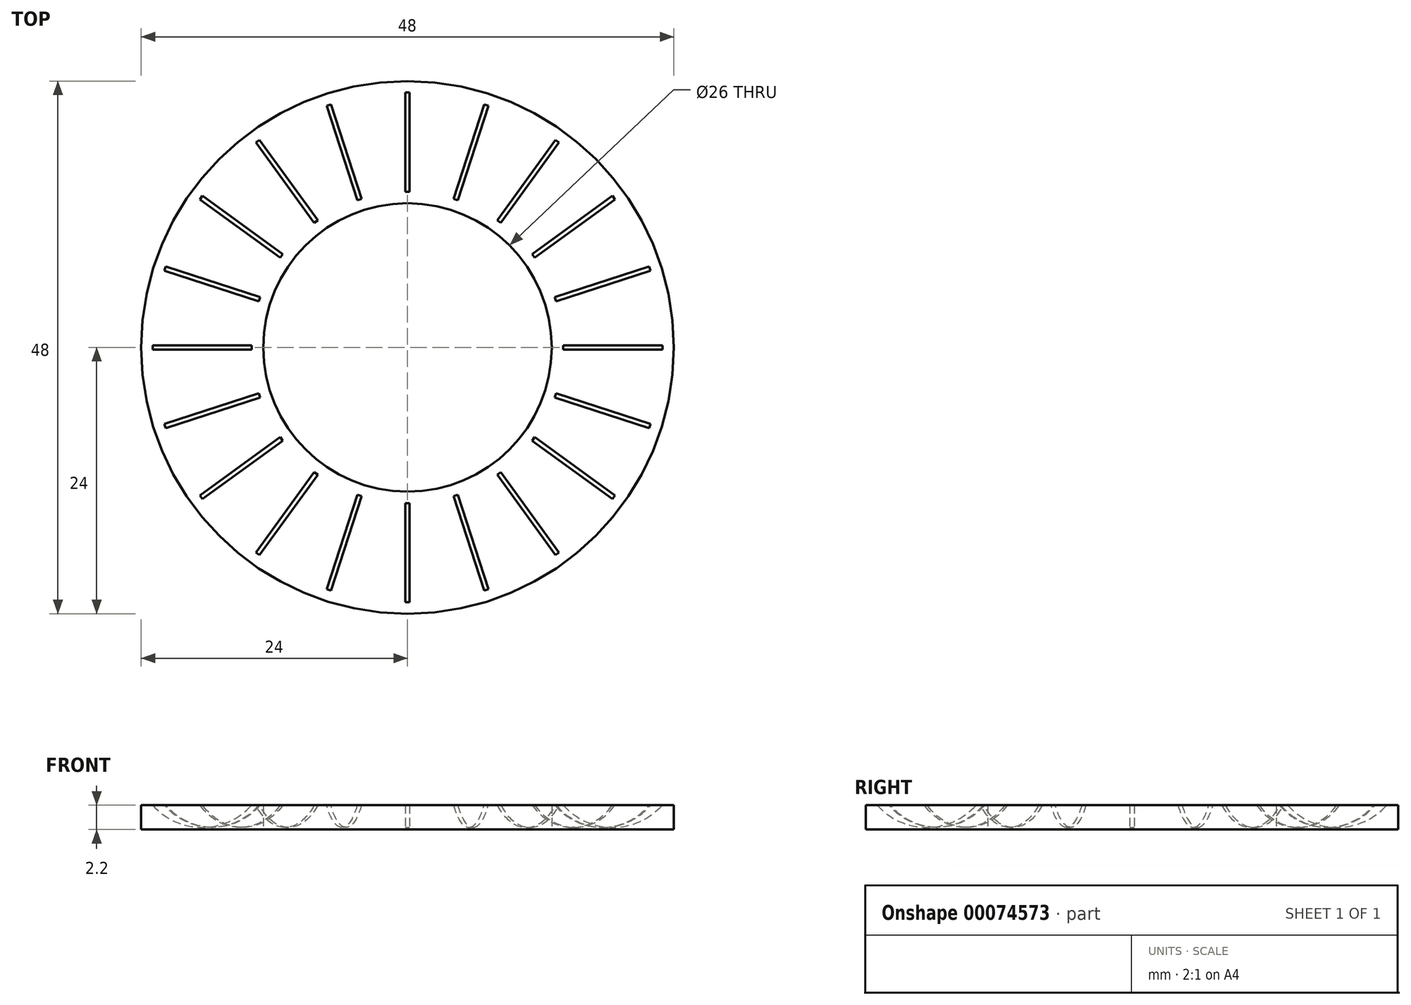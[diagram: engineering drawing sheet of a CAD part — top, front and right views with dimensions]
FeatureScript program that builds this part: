
annotation { "Feature Type Name" : "Feature", "Feature Type Description" : "" }
export const myFeature = defineFeature(function(context is Context, id is Id, definition is map)
    precondition{}
    {
        {
            var Q0;
            Q0=qCreatedBy(makeId("Top.planeOp"),FACE);
            var sketch = newSketch(context, id + "F0", { "sketchPlane" : qUnion([Q0])});
            skCircle(sketch, "E0", {"center": v(0, 0) * mm, "radius": 13 * mm});
            skCircle(sketch, "E1", {"center": v(0, 0) * mm, "radius": 24 * mm});
            skSolve(sketch);
        }
        {
            var Q0;
            Q0=makeQuery(id+"F0.imprint","IMPRINT",FACE,{"disambiguationData":[TD([[makeQuery(id+"F0.imprint","IMPRINT",EDGE,{"derivedFrom":sQuery(id+"F0.wireOp",EDGE,"E0")}),-1.0]])]});
            extrude(context, id + "F1", {"entities" : qUnion([Q0]), "depth" : 2.2 * mm});
        }
        {
            var Q0;
            Q0=qCreatedBy(makeId("Front.planeOp"),FACE);
            var sketch = newSketch(context, id + "F2", { "sketchPlane" : qUnion([Q0])});
            skLineSegment(sketch, "E2.bottom", {"start": v(0, 0) * mm, "end": v(18.5, 0) * mm, "construction": true});
            skLineSegment(sketch, "E2.top", {"start": v(0, 6.2) * mm, "end": v(18.5, 6.2) * mm, "construction": true});
            skLineSegment(sketch, "E2.left", {"start": v(0, 0) * mm, "end": v(0, 6.2) * mm, "construction": true});
            skLineSegment(sketch, "E2.right", {"start": v(18.5, 0) * mm, "end": v(18.5, 6.2) * mm, "construction": true});
            skCircle(sketch, "E3", {"center": v(18.5, 6.2) * mm, "radius": 6 * mm});
            skSolve(sketch);
        }
        {
            var Q0;
            Q0=makeQuery(id+"F2.imprint","IMPRINT",FACE,{"disambiguationData":[TD([[makeQuery(id+"F2.imprint","IMPRINT",EDGE,{"derivedFrom":sQuery(id+"F2.wireOp",EDGE,"E3")}),1.0]])]});
            extrude(context, id + "F3", {"entities" : qUnion([Q0]), "endBound" : BoundingType.SYMMETRIC, "depth" : .4 * mm});
        }
        {
            var Q0;
            Q0=makeQuery(id+"F3.opExtrude","SWEPT_BODY",BODY,{"disambiguationData":[OSD([sQuery(id+"F2.wireOp",EDGE,"E3")])]});
            var Q1;
            Q1=sQuery(id+"F2.wireOp",EDGE,"E2.left");
            circularPattern(context, id + "F4", {"entities" : qUnion([Q0]), "axis" : qUnion([Q1]), "angle" : 360 * degree, "instanceCount" : 20, "equalSpace" : true});
        }
        {
            var Q0;
            Q0=makeQuery(id+"F3.opExtrude","SWEPT_BODY",BODY,{"disambiguationData":[OSD([sQuery(id+"F2.wireOp",EDGE,"E3")])]});
            var Q1;
            Q1=makeQuery(id+"F4.opPattern","COPY",BODY,{"derivedFrom":makeQuery(id+"F3.opExtrude","SWEPT_BODY",BODY,{"disambiguationData":[OSD([sQuery(id+"F2.wireOp",EDGE,"E3")])]}),"instanceName":"18"});
            var Q2;
            Q2=makeQuery(id+"F4.opPattern","COPY",BODY,{"derivedFrom":makeQuery(id+"F3.opExtrude","SWEPT_BODY",BODY,{"disambiguationData":[OSD([sQuery(id+"F2.wireOp",EDGE,"E3")])]}),"instanceName":"16"});
            var Q3;
            Q3=makeQuery(id+"F4.opPattern","COPY",BODY,{"derivedFrom":makeQuery(id+"F3.opExtrude","SWEPT_BODY",BODY,{"disambiguationData":[OSD([sQuery(id+"F2.wireOp",EDGE,"E3")])]}),"instanceName":"15"});
            var Q4;
            Q4=makeQuery(id+"F4.opPattern","COPY",BODY,{"derivedFrom":makeQuery(id+"F3.opExtrude","SWEPT_BODY",BODY,{"disambiguationData":[OSD([sQuery(id+"F2.wireOp",EDGE,"E3")])]}),"instanceName":"17"});
            var Q5;
            Q5=makeQuery(id+"F4.opPattern","COPY",BODY,{"derivedFrom":makeQuery(id+"F3.opExtrude","SWEPT_BODY",BODY,{"disambiguationData":[OSD([sQuery(id+"F2.wireOp",EDGE,"E3")])]}),"instanceName":"19"});
            var Q6;
            Q6=makeQuery(id+"F4.opPattern","COPY",BODY,{"derivedFrom":makeQuery(id+"F3.opExtrude","SWEPT_BODY",BODY,{"disambiguationData":[OSD([sQuery(id+"F2.wireOp",EDGE,"E3")])]}),"instanceName":"13"});
            var Q7;
            Q7=makeQuery(id+"F4.opPattern","COPY",BODY,{"derivedFrom":makeQuery(id+"F3.opExtrude","SWEPT_BODY",BODY,{"disambiguationData":[OSD([sQuery(id+"F2.wireOp",EDGE,"E3")])]}),"instanceName":"11"});
            var Q8;
            Q8=makeQuery(id+"F4.opPattern","COPY",BODY,{"derivedFrom":makeQuery(id+"F3.opExtrude","SWEPT_BODY",BODY,{"disambiguationData":[OSD([sQuery(id+"F2.wireOp",EDGE,"E3")])]}),"instanceName":"8"});
            var Q9;
            Q9=makeQuery(id+"F4.opPattern","COPY",BODY,{"derivedFrom":makeQuery(id+"F3.opExtrude","SWEPT_BODY",BODY,{"disambiguationData":[OSD([sQuery(id+"F2.wireOp",EDGE,"E3")])]}),"instanceName":"12"});
            var Q10;
            Q10=makeQuery(id+"F4.opPattern","COPY",BODY,{"derivedFrom":makeQuery(id+"F3.opExtrude","SWEPT_BODY",BODY,{"disambiguationData":[OSD([sQuery(id+"F2.wireOp",EDGE,"E3")])]}),"instanceName":"14"});
            var Q11;
            Q11=makeQuery(id+"F4.opPattern","COPY",BODY,{"derivedFrom":makeQuery(id+"F3.opExtrude","SWEPT_BODY",BODY,{"disambiguationData":[OSD([sQuery(id+"F2.wireOp",EDGE,"E3")])]}),"instanceName":"9"});
            var Q12;
            Q12=makeQuery(id+"F4.opPattern","COPY",BODY,{"derivedFrom":makeQuery(id+"F3.opExtrude","SWEPT_BODY",BODY,{"disambiguationData":[OSD([sQuery(id+"F2.wireOp",EDGE,"E3")])]}),"instanceName":"10"});
            var Q13;
            Q13=makeQuery(id+"F4.opPattern","COPY",BODY,{"derivedFrom":makeQuery(id+"F3.opExtrude","SWEPT_BODY",BODY,{"disambiguationData":[OSD([sQuery(id+"F2.wireOp",EDGE,"E3")])]}),"instanceName":"7"});
            var Q14;
            Q14=makeQuery(id+"F4.opPattern","COPY",BODY,{"derivedFrom":makeQuery(id+"F3.opExtrude","SWEPT_BODY",BODY,{"disambiguationData":[OSD([sQuery(id+"F2.wireOp",EDGE,"E3")])]}),"instanceName":"5"});
            var Q15;
            Q15=makeQuery(id+"F4.opPattern","COPY",BODY,{"derivedFrom":makeQuery(id+"F3.opExtrude","SWEPT_BODY",BODY,{"disambiguationData":[OSD([sQuery(id+"F2.wireOp",EDGE,"E3")])]}),"instanceName":"3"});
            var Q16;
            Q16=makeQuery(id+"F4.opPattern","COPY",BODY,{"derivedFrom":makeQuery(id+"F3.opExtrude","SWEPT_BODY",BODY,{"disambiguationData":[OSD([sQuery(id+"F2.wireOp",EDGE,"E3")])]}),"instanceName":"4"});
            var Q17;
            Q17=makeQuery(id+"F4.opPattern","COPY",BODY,{"derivedFrom":makeQuery(id+"F3.opExtrude","SWEPT_BODY",BODY,{"disambiguationData":[OSD([sQuery(id+"F2.wireOp",EDGE,"E3")])]}),"instanceName":"2"});
            var Q18;
            Q18=makeQuery(id+"F4.opPattern","COPY",BODY,{"derivedFrom":makeQuery(id+"F3.opExtrude","SWEPT_BODY",BODY,{"disambiguationData":[OSD([sQuery(id+"F2.wireOp",EDGE,"E3")])]}),"instanceName":"1"});
            var Q19;
            Q19=makeQuery(id+"F4.opPattern","COPY",BODY,{"derivedFrom":makeQuery(id+"F3.opExtrude","SWEPT_BODY",BODY,{"disambiguationData":[OSD([sQuery(id+"F2.wireOp",EDGE,"E3")])]}),"instanceName":"6"});
            var Q20;
            Q20=makeQuery(id+"F1.opExtrude","SWEPT_BODY",BODY,{"disambiguationData":[OSD([sQuery(id+"F0.wireOp",EDGE,"E0"),sQuery(id+"F0.wireOp",EDGE,"E1")])]});
            booleanBodies(context, id + "F5", {"operationType" : BooleanOperationType.SUBTRACTION, "tools" : qUnion([Q0, Q1, Q2, Q3, Q4, Q5, Q6, Q7, Q8, Q9, Q10, Q11, Q12, Q13, Q14, Q15, Q16, Q17, Q18, Q19]), "targets" : qUnion([Q20])});
        }
    });
